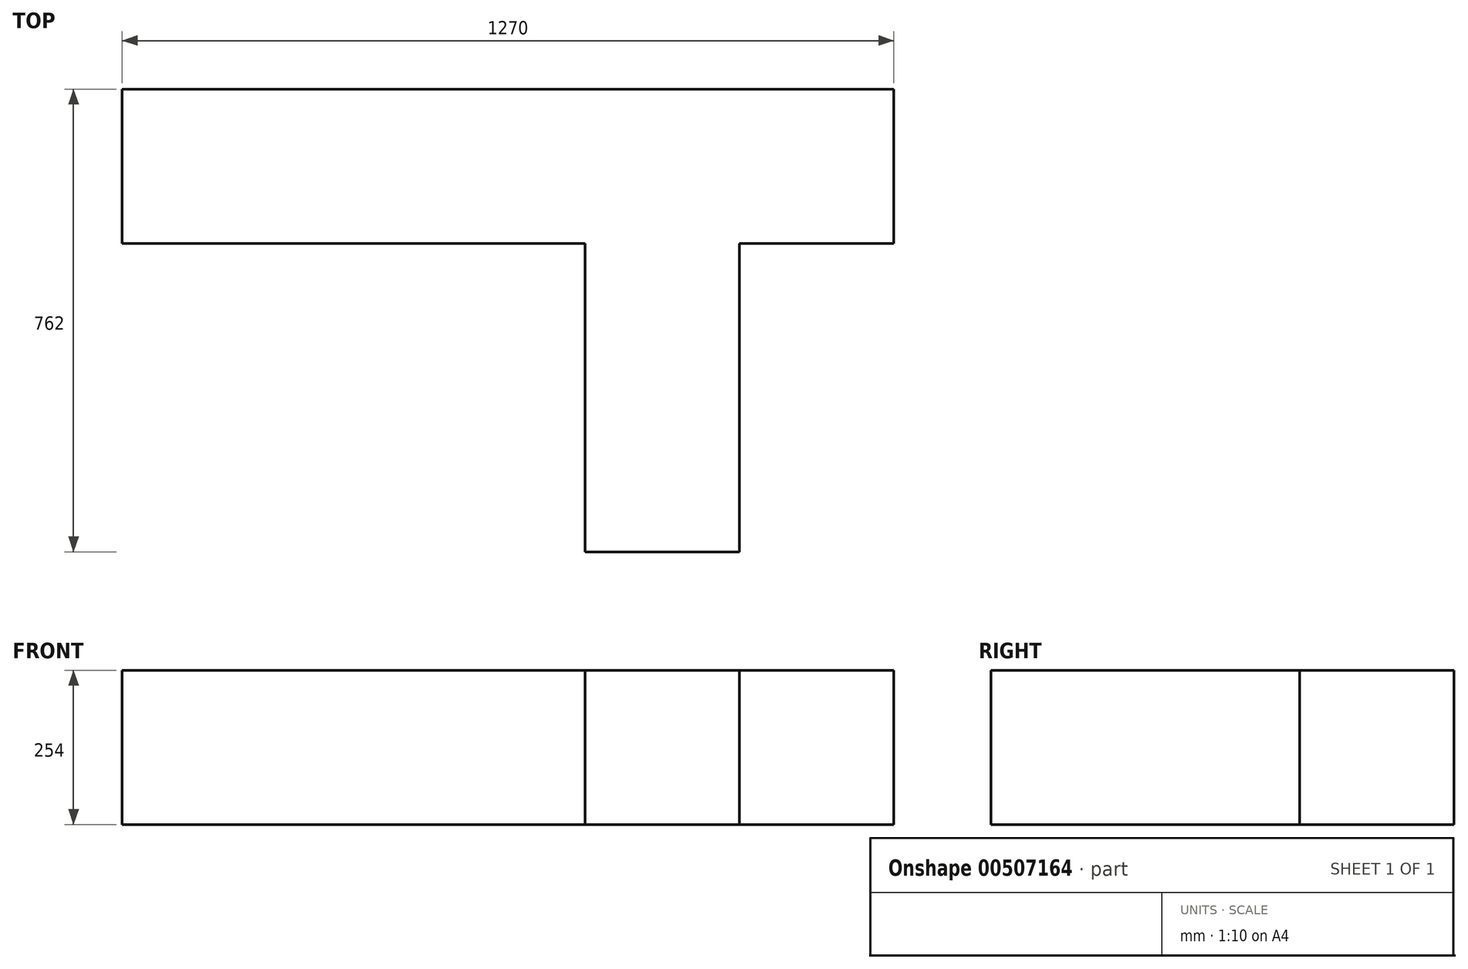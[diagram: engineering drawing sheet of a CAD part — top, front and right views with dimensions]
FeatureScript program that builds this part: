
annotation { "Feature Type Name" : "Feature", "Feature Type Description" : "" }
export const myFeature = defineFeature(function(context is Context, id is Id, definition is map)
    precondition{}
    {
        {
            var Q0;
            Q0=qCreatedBy(makeId("Top.planeOp"),FACE);
            var sketch = newSketch(context, id + "F0", { "sketchPlane" : qUnion([Q0])});
            skLineSegment(sketch, "E0", {"start": v(-337.5, 460.93) * mm, "end": v(-337.5, 206.93) * mm});
            skLineSegment(sketch, "E1", {"start": v(-337.5, 206.93) * mm, "end": v(424.5, 206.93) * mm});
            skLineSegment(sketch, "E2", {"start": v(424.5, 206.93) * mm, "end": v(424.5, -301.07) * mm});
            skLineSegment(sketch, "E3", {"start": v(424.5, -301.07) * mm, "end": v(678.5, -301.07) * mm});
            skLineSegment(sketch, "E4", {"start": v(678.5, -301.07) * mm, "end": v(678.5, 206.93) * mm});
            skLineSegment(sketch, "E5", {"start": v(678.5, 206.93) * mm, "end": v(932.5, 206.93) * mm});
            skLineSegment(sketch, "E6", {"start": v(932.5, 206.93) * mm, "end": v(932.5, 460.93) * mm});
            skLineSegment(sketch, "E7", {"start": v(932.5, 460.93) * mm, "end": v(-337.5, 460.93) * mm});
            skSolve(sketch);
        }
        {
            var Q0;
            Q0=makeQuery(id+"F0.imprint","IMPRINT",FACE,{"disambiguationData":[TD([[makeQuery(id+"F0.imprint","IMPRINT",EDGE,{"derivedFrom":sQuery(id+"F0.wireOp",EDGE,"E0")}),1.0]])]});
            extrude(context, id + "F1", {"entities" : qUnion([Q0]), "depth" : 254 * mm});
        }
    });
